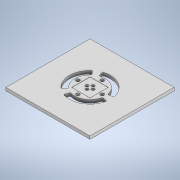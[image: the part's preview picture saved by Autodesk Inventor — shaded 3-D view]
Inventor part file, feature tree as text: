
AUTODESK INVENTOR PART (.ipt)
format: ipt  version: 2022 (Build 260153000, 153)  size: 354,304 bytes
history: native  units: in
note: dims shown in document units (in); Inventor stores cm internally (conversion verified against a paired STEP export)
features: extrude x6, sketch x6, projected_geometry x5, other x3, reference x2, chamfer x1, fillet x1, thicken_offset x1
ambient origin geometry x8: Origin, YZ Plane, XZ Plane, XY Plane, X Axis, Y Axis, Z Axis, Center Point
bodies: Solid1 (feature_tree)
feature tree (25):
  extrude  "Extrusion1"  Depth=2.2638in
  extrude  "Extrusion2"  Depth=0.1in
  chamfer  "Chamfer1"  Distance=0.05in
  extrude  "Extrusion3"  Depth=0.1in
  extrude  "Extrusion4"  Depth=0.1in
  fillet  "Fillet1"  Radius=1.0046in
  extrude  "Extrusion5"  Depth=0.05in TaperAngle=0.0deg
  thicken_offset  "Thicken1"
  extrude  "Extrusion6"  Depth=0.05in TaperAngle=45.0deg
  sketch  "Sketch1"  dims[d0=2.2638in d1=2.2638in]
  sketch  "Sketch2"  dims[d2=0.1in d3=0.0in d4=0.7546in d5=0.7546in]
  projected_geometry  "Projected Loop1"
  sketch  "Sketch3"  dims[d6=0.7546in]
  projected_geometry  "Projected Loop2"
  sketch  "Sketch4"  dims[d7=0.7546in]
  projected_geometry  "Projected Loop3"
  sketch  "Sketch5"  dims[d8=0.7546in]
  reference  "Reference1"
  reference  "Reference2"
  sketch  "Sketch6"  dims[d9=0.05in d10=0.05in d11=0.55in d12=0.55in d13=1.1811in d15=1.0046in d16=1.1811in d18=1.0046in d21=0.05in d22=0.0in d23=0.05in d24=0.125in d25=45.0deg d26=0.3in d27=0.3in d28=0.005in d29=0.0in d30=0.6in d31=0.6in d32=1.0in d33=0.0in d34=0.0in d35=120.0deg d36=120.0deg d37=0.0in d38=0.7559in d39=0.8933in d40=0.7559in d41=0.8933in d42=0.0687in d43=0.0687in d44=0.035in d45=0.05in d46=0.0in d47=1.5546in d48=1.355in d49=0.25in d50=0.25in d51=0.374in d52=0.374in d53=0.1in d54=0.1in d55=0.0in d56=0.1in d57=90.0deg d58=0.05in d59=0.05in d60=0.05in d61=1.0in d62=0.0in d63=0.1in d64=0.1in d65=0.1in d66=0.1in d67=0.1in d68=0.1in d69=0.1in d70=0.1181in d71=0.1181in]
  projected_geometry  "Projected Loop4"
  projected_geometry  "Projected Loop5"
  parser-record x1  (decoder bookkeeping rows leaked as tree rows — omitted from the tree; the rows remain in map.json)
  other  "CubeAssembly.iam"
  other  "SpringPotBottom:2"
note: 1 file-system path scrubbed to <path> (originals preserved in map.json)
